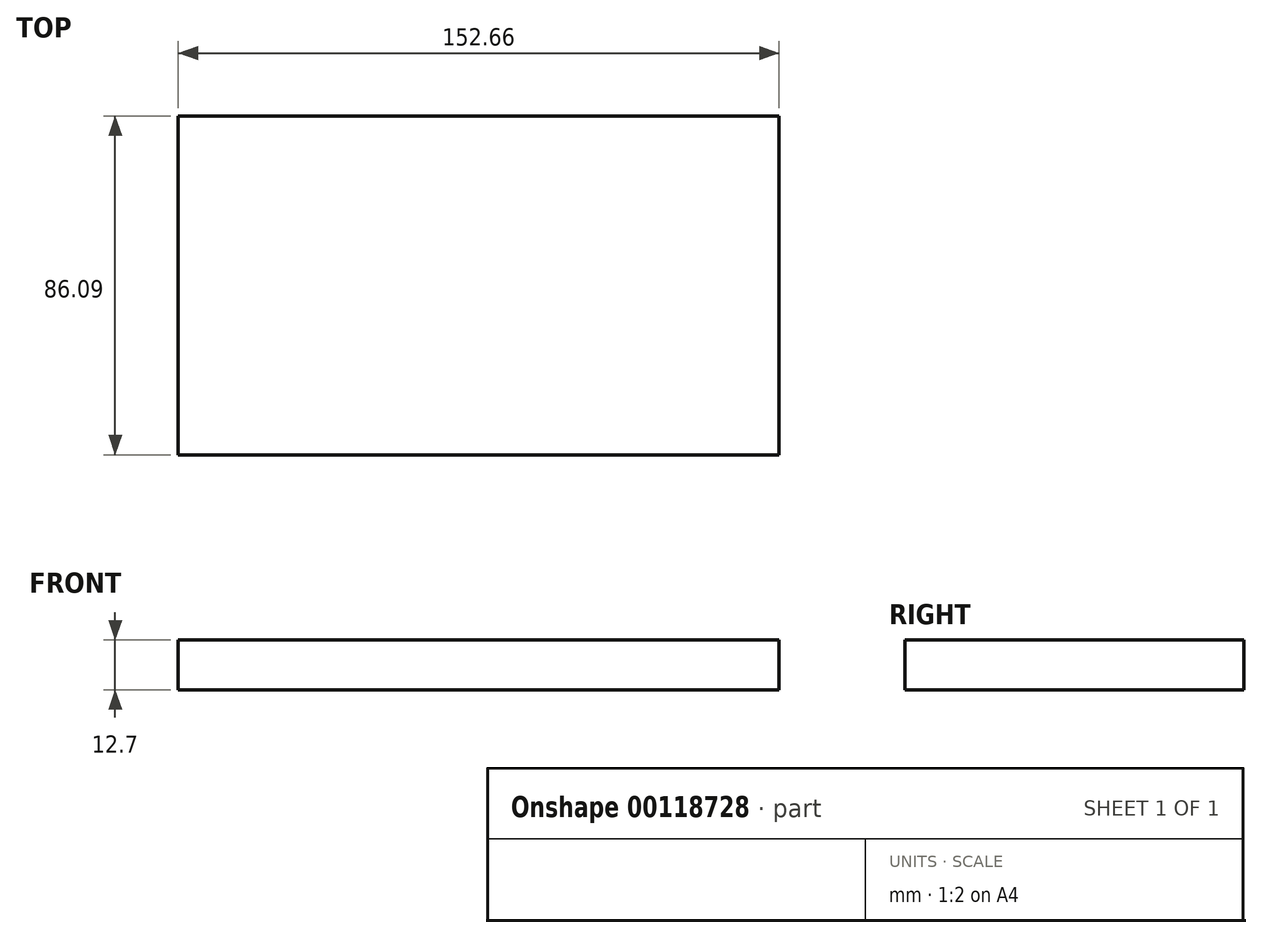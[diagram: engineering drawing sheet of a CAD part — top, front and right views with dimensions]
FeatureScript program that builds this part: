
annotation { "Feature Type Name" : "Feature", "Feature Type Description" : "" }
export const myFeature = defineFeature(function(context is Context, id is Id, definition is map)
    precondition{}
    {
        {
            var Q0;
            Q0=qCreatedBy(makeId("Top.planeOp"),FACE);
            var sketch = newSketch(context, id + "F0", { "sketchPlane" : qUnion([Q0])});
            skLineSegment(sketch, "E0.bottom", {"start": v(-76.93, 56) * mm, "end": v(75.73, 56) * mm});
            skLineSegment(sketch, "E0.top", {"start": v(-76.93, -30.08) * mm, "end": v(75.73, -30.08) * mm});
            skLineSegment(sketch, "E0.left", {"start": v(-76.93, 56) * mm, "end": v(-76.93, -30.08) * mm});
            skLineSegment(sketch, "E0.right", {"start": v(75.73, 56) * mm, "end": v(75.73, -30.08) * mm});
            skSolve(sketch);
        }
        {
            var Q0;
            Q0=makeQuery(id+"F0.imprint","IMPRINT",FACE,{"disambiguationData":[TD([[makeQuery(id+"F0.imprint","IMPRINT",EDGE,{"derivedFrom":sQuery(id+"F0.wireOp",EDGE,"E0.bottom")}),-1.0]])]});
            extrude(context, id + "F1", {"entities" : qUnion([Q0]), "depth" : 12.7 * mm});
        }
    });
